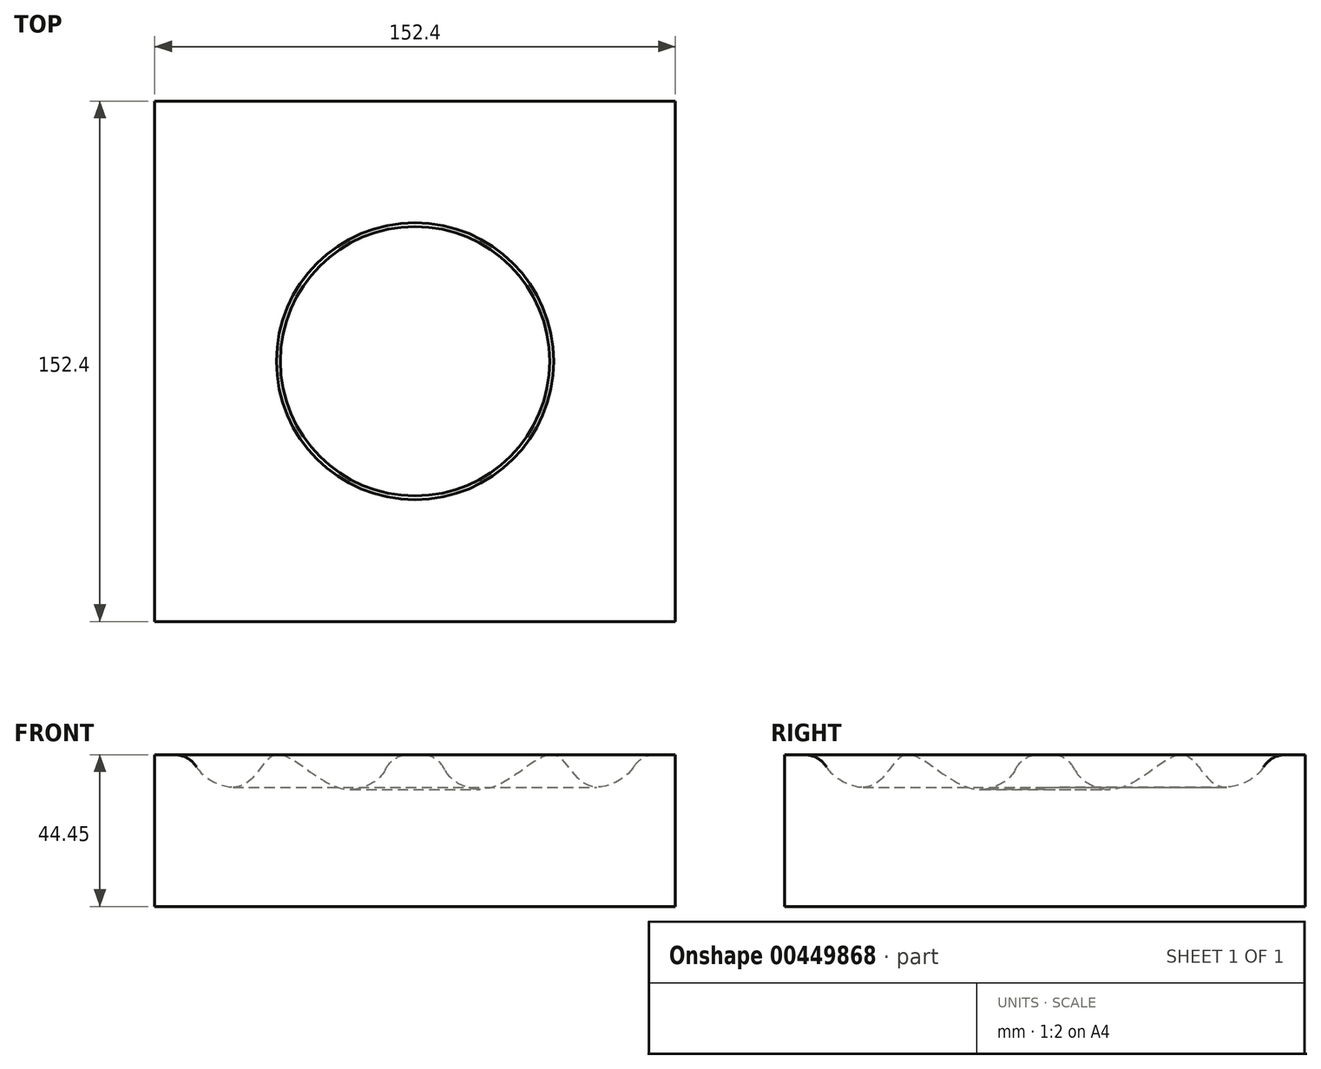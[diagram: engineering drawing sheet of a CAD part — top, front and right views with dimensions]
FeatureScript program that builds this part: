
annotation { "Feature Type Name" : "Feature", "Feature Type Description" : "" }
export const myFeature = defineFeature(function(context is Context, id is Id, definition is map)
    precondition{}
    {
        {
            var Q0;
            Q0=qCreatedBy(makeId("Top.planeOp"),FACE);
            var sketch = newSketch(context, id + "F0", { "sketchPlane" : qUnion([Q0])});
            skLineSegment(sketch, "E0.bottom", {"start": v(76.2, -76.2) * mm, "end": v(-76.2, -76.2) * mm});
            skLineSegment(sketch, "E0.top", {"start": v(76.2, 76.2) * mm, "end": v(-76.2, 76.2) * mm});
            skLineSegment(sketch, "E0.left", {"start": v(76.2, -76.2) * mm, "end": v(76.2, 76.2) * mm});
            skLineSegment(sketch, "E0.right", {"start": v(-76.2, -76.2) * mm, "end": v(-76.2, 76.2) * mm});
            skPoint(sketch, "E0.middle", {"position": v(0, 0) * mm});
            skSolve(sketch);
        }
        {
            var Q0;
            Q0 = qSketchRegion(id + "F0", true);
            extrude(context, id + "F1", {"entities" : qUnion([Q0]), "depth" : 44.45 * mm});
        }
        {
            var Q0;
            Q0=qCreatedBy(makeId("Front.planeOp"),FACE);
            var sketch = newSketch(context, id + "F2", { "sketchPlane" : qUnion([Q0])});
            skLineSegment(sketch, "E1", {"start": v(-64.3, 44.45) * mm, "end": v(-64.3, 44.45) * mm});
            skLineSegment(sketch, "E2", {"start": v(-64.3, 44.45) * mm, "end": v(-64.3, 0) * mm, "construction": true});
            skLineSegment(sketch, "E3", {"start": v(0, 0) * mm, "end": v(0, 44.45) * mm, "construction": true});
            skLineSegment(sketch, "E4", {"start": v(-64.3, 44.45) * mm, "end": v(-48.13, 0) * mm, "construction": true});
            skFitSpline(sketch, "E5", {"points": [v(-64.3, 44.45) * mm, v(-52.03, 35.03) * mm, v(-40.55, 44.45) * mm, v(-19.06, 34.24) * mm, v(-9.03, 44.45) * mm, v(-64.3, 44.45) * mm]});
            skSolve(sketch);
        }
        {
            var Q0;
            Q0 = qSketchRegion(id + "F2", true);
            var Q1;
            Q1=sQuery(id+"F2.wireOp",EDGE,"E3");
            revolve(context, id + "F3", {"operationType" : NewBodyOperationType.REMOVE, "entities" : qUnion([Q0]), "axis" : qUnion([Q1]), "revolveType" : RevolveType.FULL, "oppositeDirection" : true});
        }
        {
            var Q0;
            Q0=makeQuery(id+"F3.boolean.opBoolean","INTERSECT",EDGE,{"disambiguationData":[OD(1.0)],"derivedFrom":[makeQuery(id+"F1.opExtrude","CAP_FACE",FACE,{"disambiguationData":[OSD([sQuery(id+"F0.wireOp",EDGE,"E0.bottom"),sQuery(id+"F0.wireOp",EDGE,"E0.top"),sQuery(id+"F0.wireOp",EDGE,"E0.left"),sQuery(id+"F0.wireOp",EDGE,"E0.right")])],"isStart":false}),makeQuery(id+"F3.opRevolve","SWEPT_FACE",FACE,{"disambiguationData":[OSD([sQuery(id+"F2.wireOp",EDGE,"E5")])]})]});
            var Q1;
            Q1=makeQuery(id+"F3.boolean.opBoolean","INTERSECT",EDGE,{"disambiguationData":[OD(0.0)],"derivedFrom":[makeQuery(id+"F1.opExtrude","CAP_FACE",FACE,{"disambiguationData":[OSD([sQuery(id+"F0.wireOp",EDGE,"E0.bottom"),sQuery(id+"F0.wireOp",EDGE,"E0.top"),sQuery(id+"F0.wireOp",EDGE,"E0.left"),sQuery(id+"F0.wireOp",EDGE,"E0.right")])],"isStart":false}),makeQuery(id+"F3.opRevolve","SWEPT_FACE",FACE,{"disambiguationData":[OSD([sQuery(id+"F2.wireOp",EDGE,"E5")])]})]});
            fillet(context, id + "F4", {"entities" : qUnion([Q0, Q1]), "radius" : 7.62 * mm, "tangentPropagation" : true, "allowEdgeOverflow" : false});
        }
    });
